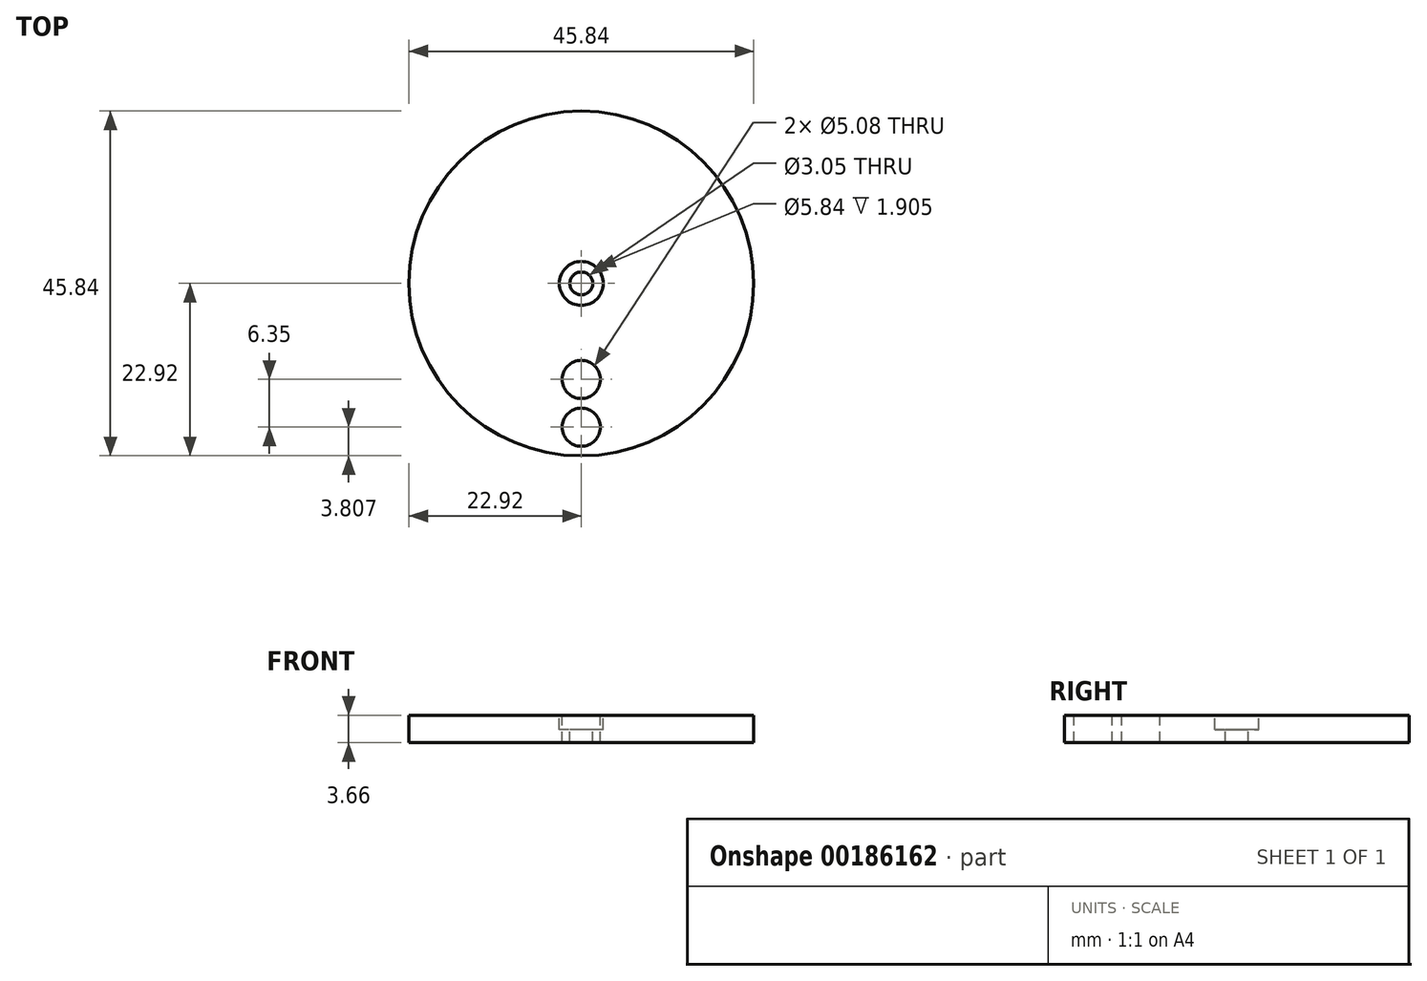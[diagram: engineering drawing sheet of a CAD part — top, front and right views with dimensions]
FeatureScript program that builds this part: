
annotation { "Feature Type Name" : "Feature", "Feature Type Description" : "" }
export const myFeature = defineFeature(function(context is Context, id is Id, definition is map)
    precondition{}
    {
        {
            var Q0;
            Q0=qCreatedBy(makeId("Top.planeOp"),FACE);
            var sketch = newSketch(context, id + "F0", { "sketchPlane" : qUnion([Q0])});
            skCircle(sketch, "E0", {"center": v(0, 0) * mm, "radius": 22.92 * mm});
            skSolve(sketch);
        }
        {
            var Q0;
            Q0 = qSketchRegion(id + "F0", true);
            extrude(context, id + "F1", {"entities" : qUnion([Q0]), "depth" : 3.66 * mm});
        }
        {
            var Q0;
            Q0=makeQuery(id+"F1.opExtrude","CAP_FACE",FACE,{"disambiguationData":[OSD([sQuery(id+"F0.wireOp",EDGE,"E0")])],"isStart":false});
            var sketch = newSketch(context, id + "F2", { "sketchPlane" : qUnion([Q0])});
            skCircle(sketch, "E1", {"center": v(0, -19.11) * mm, "radius": 2.54 * mm});
            skCircle(sketch, "E2", {"center": v(0, -12.76) * mm, "radius": 2.54 * mm});
            skCircle(sketch, "E3", {"center": v(0, 0) * mm, "radius": 1.52 * mm});
            skSolve(sketch);
        }
        {
            var Q0;
            Q0=makeQuery(id+"F2.imprint","IMPRINT",FACE,{"disambiguationData":[TD([[makeQuery(id+"F2.imprint","IMPRINT",EDGE,{"derivedFrom":sQuery(id+"F2.wireOp",EDGE,"E1")}),1.0]])]});
            var Q1;
            Q1=makeQuery(id+"F2.imprint","IMPRINT",FACE,{"disambiguationData":[TD([[makeQuery(id+"F2.imprint","IMPRINT",EDGE,{"derivedFrom":sQuery(id+"F2.wireOp",EDGE,"chzQAhsX-7qym-horA-LkBO-DpAyGmkTq33F")}),1.0]])]});
            var Q2;
            Q2=makeQuery(id+"F2.imprint","IMPRINT",FACE,{"disambiguationData":[TD([[makeQuery(id+"F2.imprint","IMPRINT",EDGE,{"derivedFrom":sQuery(id+"F2.wireOp",EDGE,"E2")}),1.0]])]});
            extrude(context, id + "F3", {"entities" : qUnion([Q0, Q1, Q2]), "operationType" : NewBodyOperationType.REMOVE, "endBound" : BoundingType.THROUGH_ALL, "oppositeDirection" : true, "depth" : 50.8 * mm});
        }
        {
            var Q0;
            Q0=makeQuery(id+"F2.imprint","IMPRINT",FACE,{"disambiguationData":[TD([[makeQuery(id+"F2.imprint","IMPRINT",EDGE,{"derivedFrom":sQuery(id+"F2.wireOp",EDGE,"E3")}),1.0]])]});
            extrude(context, id + "F4", {"entities" : qUnion([Q0]), "operationType" : NewBodyOperationType.REMOVE, "oppositeDirection" : true, "depth" : 25.4 * mm});
        }
        {
            var Q0;
            Q0=makeQuery(id+"F1.opExtrude","CAP_FACE",FACE,{"disambiguationData":[OSD([sQuery(id+"F0.wireOp",EDGE,"E0")])],"isStart":false});
            var sketch = newSketch(context, id + "F5", { "sketchPlane" : qUnion([Q0])});
            skCircle(sketch, "E4", {"center": v(0, 0) * mm, "radius": 2.92 * mm});
            skSolve(sketch);
        }
        {
            var Q0;
            Q0=makeQuery(id+"F5.imprint","IMPRINT",FACE,{"disambiguationData":[TD([[makeQuery(id+"F5.imprint","IMPRINT",EDGE,{"derivedFrom":sQuery(id+"F5.wireOp",EDGE,"E4")}),1.0]])]});
            extrude(context, id + "F6", {"entities" : qUnion([Q0]), "operationType" : NewBodyOperationType.REMOVE, "oppositeDirection" : true, "depth" : 1.9 * mm});
        }
    });
